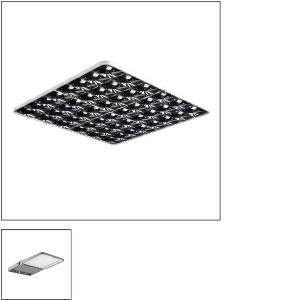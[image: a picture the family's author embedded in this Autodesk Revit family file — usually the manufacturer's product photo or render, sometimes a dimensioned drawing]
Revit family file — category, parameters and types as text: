
# Revit family: siteco_mirrortec_r__indoor___rs05_5nw14093qc_3e65
name_source: partatom
category: Lighting Fixtures
units: mm (PartAtom-declared; Revit-internal decimal feet)

## family parameters
Cut with Voids When Loaded = No
Host = Face
Light Source = No
Part Type = Normal
Room Calculation Point = No
Round Connector Dimension = Use Diameter
Shared = No

## types (1)
- 5XA7682G2H2AC (1 x LED, 33940 lm, 305.7 W, 4000K)
    Apparent Load = 306 VA
    CIE Flux Codes = 47 83 98 53 100
    Color Rendering = 70
    Color Temperature = 4000K
    Default Elevation = 1800 mm
    Description = secondary reflector, for Siteco Mirrortec® Indoor, wire hanger, housing, square, of aluminium, coated, metallic grey (RAL 9006), fresnel reflector 100, of PMMA, aluminized, highly specular, light point resolution, fresnel structure, length: 1.200 mm, width: 1.200 mm

Light Distribution: RS05
    Height = 12 mm  [stored 0.0393701 ft]
    Lamp = 1 x LED
    Lamp Light Flux = 33940 lm
    Lamp Power = 305.7 W
    Lamp count = 1
    Length = 1221 mm
    Luminous efficacy = 111 lm/W
    Manufacturer = Siteco
    ModVariant = No
    Model = 5NW14093QC
    Mounting Place = Ceiling
    Mounting Type = Pendant
    Number of Poles = 1
    OnlyDefault = Yes
    Power Factor = 1
    Product Name = Siteco Mirrortec® Indoor | RS05
    Product group = secondary reflector
    ProductGroupID = 910
    Protection Class = Protection class II
    Protection Degree = IP 66
    RLX_Detail_Level = 1
    RlxData = <blob elided: 124753 chars, md5=636707cb>
    Socket = socket
    Standby Power = 0 W
    System Light Flux = 33939 lm
    System Power = 306 W
    Type Comments = Floodlight FL 20 midi, floodlight, primary light control with lens, of plastic, primary optical cover: protective disc, of toughened safety glass, transparent, light distribution: RS05, light emission: direct distribution, primary light characteristic: rotationally symmetric, installation type: surface-mounted, LED High Power LED, rated luminous flux: 38.380 lm, light colour: 740, colour temperature: 4000K, control gear: ECG Plus, control: overheat protection, power reduction, digital communication interface, time-dependent luminous flux control, flexible luminous flux parameterisation, electronic power reduction, with terminal, 10-pole, max. 2.5mm², mains connection: 220..240V, AC, 50/60Hz, rated input power: 306W, LED unit, of diecast aluminium, powder-coated, Siteco® metallic grey (DB 702S), length: 731 mm, width: 450 mm, height: 76mm, housing frame, of diecast aluminium, powder-coated, Siteco® metallic grey (DB 702S), wall fastening, DALIprotection rating (complete): IP66, insulation class (complete): insulation class II (safety insulation), certification: CE, ENEC, VDE, protection symbol: D, permissible ambient temperature for indoor applications: -40..+40°C, permissible ambient temperature for outdoor applications: -40..+50°C, standard: DIN EN 12944, packaging unit: 1 piece

individual setting: distance floodlight mirror = 3,5m / reflector tilt = 5°
    Type Image = l_577132_1005944.jpg
    URL = http://relux.com
    VarID = 5xa7682g2h2ac@adj_128667
    Voltage = 0 V
    Weight = 0.00 kg
    Width = 1221 mm

note: [stored X ft] marks values corroborated as IEEE doubles in the binary element streams (Revit-internal decimal feet)

## geometry (parser evidence)
native form markers: Blend x4, Sweep x11
no freeform markers — native parametric forms only
